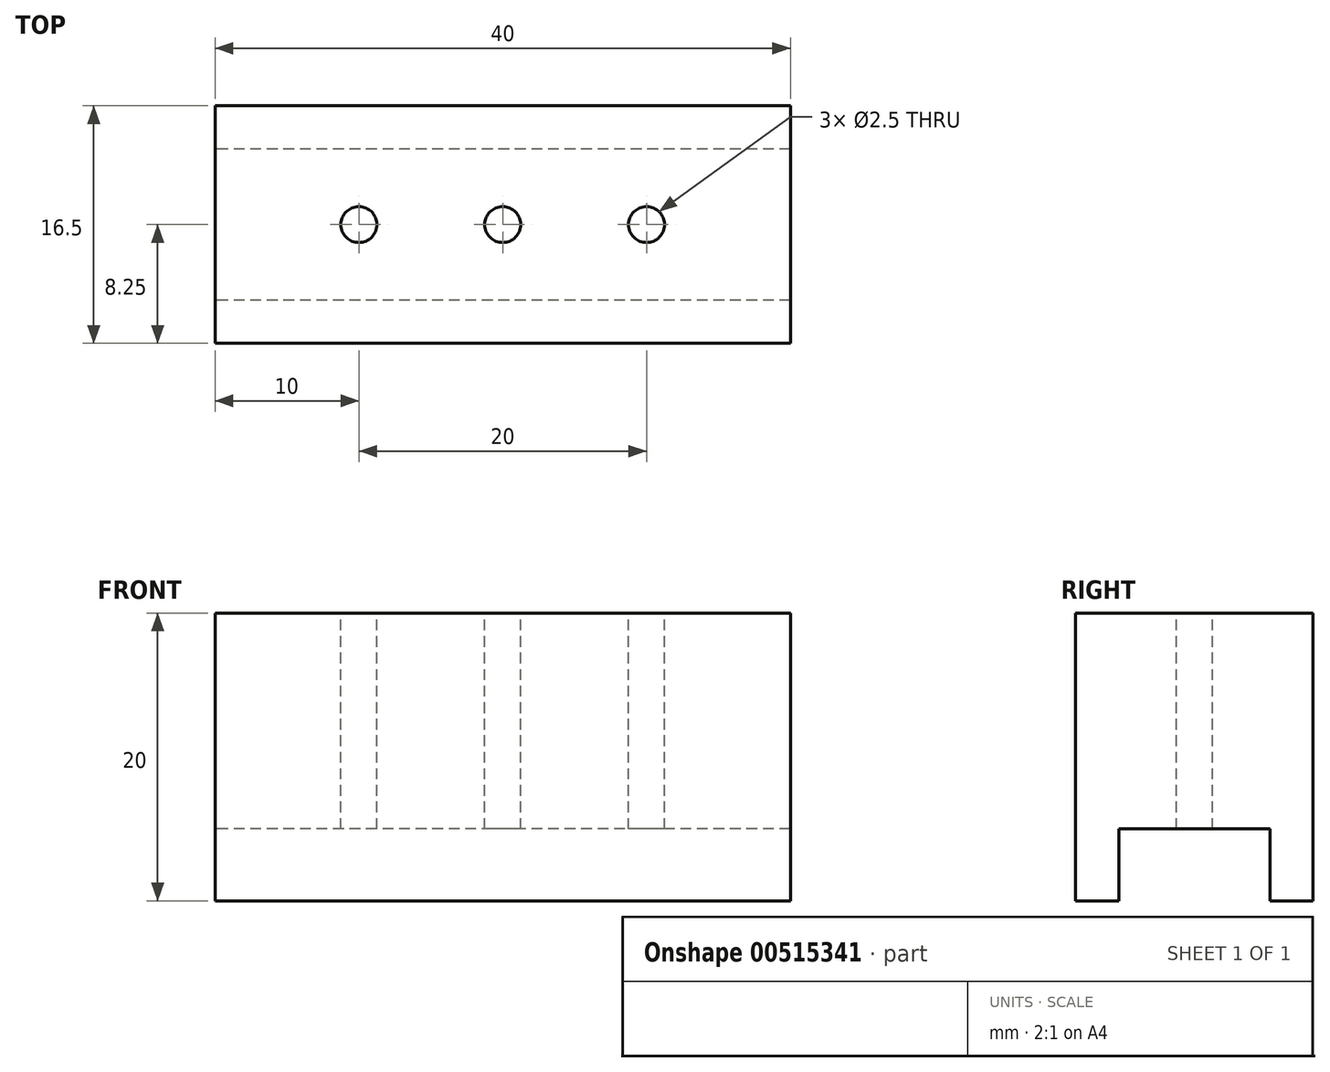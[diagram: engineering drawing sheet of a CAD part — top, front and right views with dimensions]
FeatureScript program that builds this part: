
annotation { "Feature Type Name" : "Feature", "Feature Type Description" : "" }
export const myFeature = defineFeature(function(context is Context, id is Id, definition is map)
    precondition{}
    {
        {
            var Q0;
            Q0=qCreatedBy(makeId("Top.planeOp"),FACE);
            var sketch = newSketch(context, id + "F0", { "sketchPlane" : qUnion([Q0])});
            skLineSegment(sketch, "E0.bottom", {"start": v(20, -8.25) * mm, "end": v(-20, -8.25) * mm});
            skLineSegment(sketch, "E0.top", {"start": v(20, 8.25) * mm, "end": v(-20, 8.25) * mm});
            skLineSegment(sketch, "E0.left", {"start": v(20, -8.25) * mm, "end": v(20, 8.25) * mm});
            skLineSegment(sketch, "E0.right", {"start": v(-20, -8.25) * mm, "end": v(-20, 8.25) * mm});
            skPoint(sketch, "E0.middle", {"position": v(0, 0) * mm});
            skLineSegment(sketch, "E1.bottom", {"start": v(20, -5.25) * mm, "end": v(-20, -5.25) * mm});
            skLineSegment(sketch, "E1.top", {"start": v(20, 5.25) * mm, "end": v(-20, 5.25) * mm});
            skLineSegment(sketch, "E1.left", {"start": v(20, -5.25) * mm, "end": v(20, 5.25) * mm});
            skLineSegment(sketch, "E1.right", {"start": v(-20, -5.25) * mm, "end": v(-20, 5.25) * mm});
            skSolve(sketch);
        }
        {
            var Q0;
            {var subQ0=sQuery(id+"F0.wireOp",EDGE,"E0.top");Q0=makeQuery(id+"F0.imprint","IMPRINT",FACE,{"disambiguationData":[TD([[makeQuery(id+"F0.imprint","IMPRINT",EDGE,{"derivedFrom":subQ0}),1.0]])]});}
            var Q1;
            Q1=makeQuery(id+"F0.imprint","IMPRINT",FACE,{"disambiguationData":[TD([[makeQuery(id+"F0.imprint","IMPRINT",EDGE,{"derivedFrom":sQuery(id+"F0.wireOp",EDGE,"E1.bottom")}),-1.0]])]});
            var Q2;
            {var subQ0=sQuery(id+"F0.wireOp",EDGE,"E0.bottom");Q2=makeQuery(id+"F0.imprint","IMPRINT",FACE,{"disambiguationData":[TD([[makeQuery(id+"F0.imprint","IMPRINT",EDGE,{"derivedFrom":subQ0}),-1.0]])]});}
            extrude(context, id + "F1", {"entities" : qUnion([Q0, Q1, Q2]), "depth" : 20 * mm, "offsetDistance" : 25 * mm});
        }
        {
            var Q0;
            Q0=makeQuery(id+"F0.imprint","IMPRINT",FACE,{"disambiguationData":[TD([[makeQuery(id+"F0.imprint","IMPRINT",EDGE,{"derivedFrom":sQuery(id+"F0.wireOp",EDGE,"E1.bottom")}),-1.0]])]});
            extrude(context, id + "F2", {"entities" : qUnion([Q0]), "operationType" : NewBodyOperationType.REMOVE, "depth" : 5 * mm, "offsetDistance" : 25 * mm});
        }
        {
            var Q0;
            Q0=makeQuery(id+"F1.opExtrude","CAP_FACE",FACE,{"disambiguationData":[OSD([sQuery(id+"F0.wireOp",EDGE,"E0.bottom"),sQuery(id+"F0.wireOp",EDGE,"E0.top"),sQuery(id+"F0.wireOp",EDGE,"E0.left"),sQuery(id+"F0.wireOp",EDGE,"E0.right"),sQuery(id+"F0.wireOp",EDGE,"E1.left"),sQuery(id+"F0.wireOp",EDGE,"E1.right")])],"isStart":false});
            var sketch = newSketch(context, id + "F3", { "sketchPlane" : qUnion([Q0])});
            skCircle(sketch, "E2", {"center": v(0, 0) * mm, "radius": 1.25 * mm});
            skCircle(sketch, "E3", {"center": v(10, 0) * mm, "radius": 1.25 * mm});
            skCircle(sketch, "E4", {"center": v(-10, 0) * mm, "radius": 1.25 * mm});
            skSolve(sketch);
        }
        {
            var Q0;
            Q0=makeQuery(id+"F3.imprint","IMPRINT",FACE,{"disambiguationData":[TD([[makeQuery(id+"F3.imprint","IMPRINT",EDGE,{"derivedFrom":sQuery(id+"F3.wireOp",EDGE,"E2")}),1.0]])]});
            extrude(context, id + "F4", {"entities" : qUnion([Q0]), "operationType" : NewBodyOperationType.REMOVE, "endBound" : BoundingType.THROUGH_ALL, "oppositeDirection" : true, "depth" : 25 * mm, "offsetDistance" : 25 * mm});
        }
        {
            var Q0;
            Q0=makeQuery(id+"F3.imprint","IMPRINT",FACE,{"disambiguationData":[TD([[makeQuery(id+"F3.imprint","IMPRINT",EDGE,{"derivedFrom":sQuery(id+"F3.wireOp",EDGE,"E3")}),1.0]])]});
            var Q1;
            Q1=makeQuery(id+"F3.imprint","IMPRINT",FACE,{"disambiguationData":[TD([[makeQuery(id+"F3.imprint","IMPRINT",EDGE,{"derivedFrom":sQuery(id+"F3.wireOp",EDGE,"E2")}),1.0]])]});
            var Q2;
            Q2=makeQuery(id+"F3.imprint","IMPRINT",FACE,{"disambiguationData":[TD([[makeQuery(id+"F3.imprint","IMPRINT",EDGE,{"derivedFrom":sQuery(id+"F3.wireOp",EDGE,"E4")}),1.0]])]});
            extrude(context, id + "F5", {"entities" : qUnion([Q0, Q1, Q2]), "operationType" : NewBodyOperationType.REMOVE, "endBound" : BoundingType.THROUGH_ALL, "oppositeDirection" : true, "depth" : 25 * mm, "offsetDistance" : 25 * mm});
        }
    });
